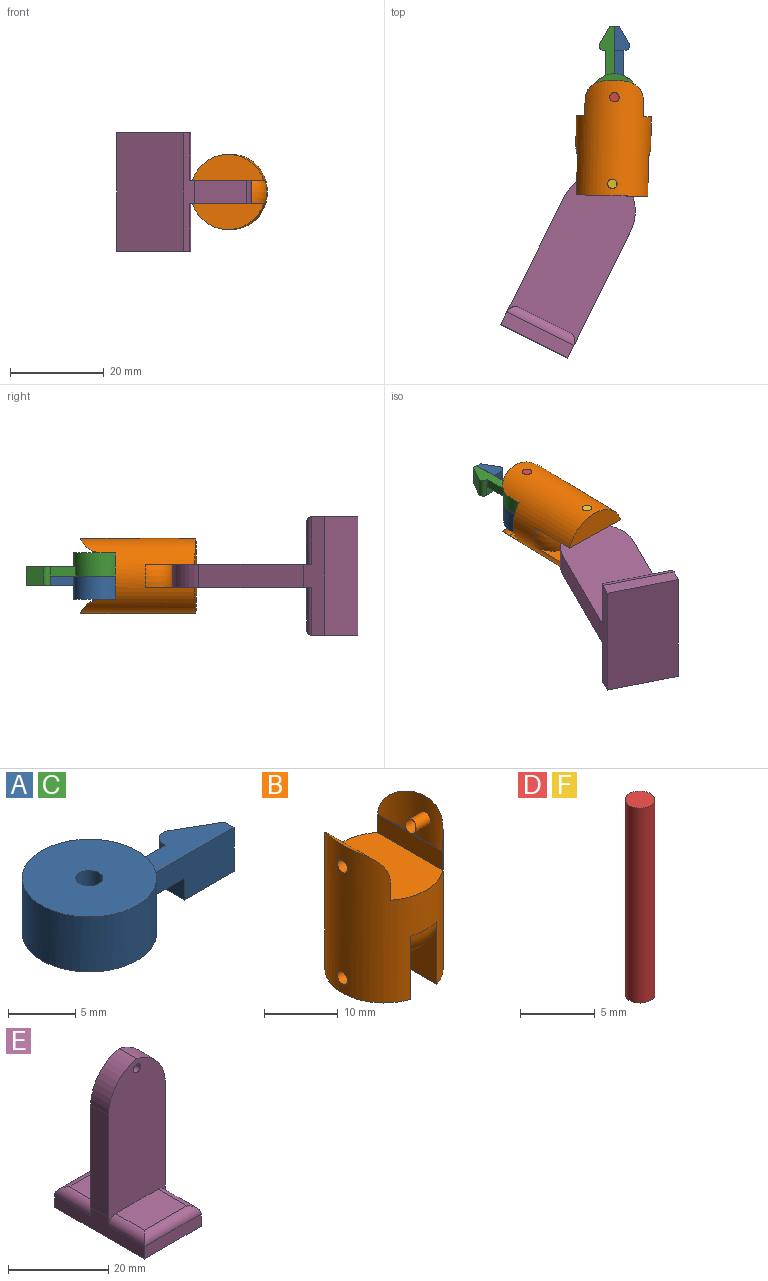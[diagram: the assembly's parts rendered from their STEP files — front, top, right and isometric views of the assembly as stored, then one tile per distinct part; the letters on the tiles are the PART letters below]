
ASSEMBLY  parts=6 mates=4
PART A: 12 faces, bbox 20.2x10x7 mm
  f0: plane 10.2x4mm, normal (0,-1,0), area 30.8mm2, adj f2,f3,f4,f6,f7,f9
  f1: plane 5.42x2mm, normal (0,1,0), area 10.8mm2, adj f2,f3,f4,f6
  f2: plane 10.61x3.27mm, normal (0,0,1), area 22.6mm2, adj f0,f1,f4,f6,f7,f8,f10
  f3: plane 15x10mm, normal (0,0,-1), area 85.7mm2, adj f0,f1,f4,f6,f11
  f4: cylinder r=5mm len=10mm, axis (0,0,-1), area 153mm2, adj f0,f1,f2,f3,f5
  f5: plane 10x10mm, normal (0,0,1), area 75.4mm2, adj f4,f11
  f6: plane 4x2.27mm, normal (-1,0,0), area 5.1mm2, adj f0,f1,f2,f3,f9,f10
  f7: plane 4x1mm, normal (1,0,0), area 4mm2, adj f0,f2,f8,f9
  f8: plane 4x3.7mm, normal (0.5,0.87,0), area 17.1mm2, adj f2,f7,f9,f10
  f9: plane 5.2x3.27mm, normal (0,0,-1), area 12.3mm2, adj f0,f6,f7,f8,f10
  f10: cylinder r=1mm len=4mm, axis (0,0,-1), area 8.4mm2, adj f2,f6,f8,f9
  f11: cylinder r=1mm len=5mm, axis (0,0,-1), area 31.4mm2, adj f3,f5
PART B: 19 faces, bbox 16x16x24.6 mm
  f0: cylinder r=8mm len=24.58mm, axis (0,0,-1), area 929mm2, adj f1,f2,f3,f5,f6,f7,f9,f10
  f1: cylinder r=1mm len=5.5mm, axis (1,0,0), area 34.4mm2, adj f0,f15
  f2: cylinder r=1mm len=5.44mm, axis (1,0,0), area 34.2mm2, adj f0,f6
  f3: cylinder r=1mm len=3mm, axis (-1,0,0), area 17.7mm2, adj f0,f4
  f4: cylinder r=5mm len=2mm, axis (0,1,0), area 3.2mm2, adj f3
  f5: plane 15.2x5.5mm, normal (0,0,-1), area 61.2mm2, adj f0,f6
  f6: plane 15.2x10.5mm, normal (-1,0,0), area 87mm2, adj f0,f2,f5,f7,f16
  f7: torus R=2.5mm, axis (0,0,-1), area 45.6mm2, adj f0,f6,f8,f15
  f8: plane 5x5mm, normal (0,0,-1), area 19.6mm2, adj f7,f16
  f9: cylinder r=5mm len=12.49mm, axis (0,-1,0), area 57.7mm2, adj f0,f10
  f10: plane 12.49x3mm, normal (-1,0,0), area 37.5mm2, adj f0,f9,f11
  f11: plane 16x10mm, normal (0,0,1), area 148.9mm2, adj f0,f10,f13
  f12: cylinder r=5mm len=12.49mm, axis (0,1,0), area 57.7mm2, adj f0,f13
  f13: plane 12.49x3mm, normal (1,0,0), area 37.5mm2, adj f0,f11,f12
  f14: plane 15.2x5.5mm, normal (0,0,-1), area 61.2mm2, adj f0,f15
  f15: plane 15.2x10.5mm, normal (1,0,0), area 87mm2, adj f0,f1,f7,f14,f16
  f16: torus R=2.5mm, axis (0,0,-1), area 45.6mm2, adj f0,f6,f8,f15
  f17: cylinder r=5mm len=2mm, axis (0,-1,0), area 3.2mm2, adj f18
  f18: cylinder r=1mm len=2.94mm, axis (-1,0,0), area 18.1mm2, adj f0,f17
PART C: same geometry as A
PART D: 3 faces, bbox 2x2x16 mm
  f0: cylinder r=1mm len=16mm, axis (0,0,-1), area 100.5mm2, adj f1,f2
  f1: plane 2x2mm, normal (0,0,1), area 3.1mm2, adj f0
  f2: plane 2x2mm, normal (0,0,-1), area 3.1mm2, adj f0
PART E: 20 faces, bbox 16x25.3x39.8 mm
  f0: plane 25.01x5.01mm, normal (1,0,0), area 125mm2, adj f1,f3,f5,f8
  f1: plane 36.8x16mm, normal (0,1,0), area 515.6mm2, adj f0,f2,f4,f5,f6,f7,f8,f10
  f2: plane 25.01x5.01mm, normal (-1,0,0), area 125mm2, adj f1,f3,f6,f10
  f3: plane 36.8x16mm, normal (0,-1,0), area 515.9mm2, adj f0,f2,f4,f5,f6,f8,f10,f13
  f4: cylinder r=1mm len=5mm, axis (0,1,0), area 31.4mm2, adj f1,f3
  f5: cylinder r=10mm len=9.8mm, axis (0,-1,0), area 68.5mm2, adj f0,f1,f3,f6
  f6: cylinder r=10mm len=9.8mm, axis (0,1,0), area 68.5mm2, adj f1,f2,f3,f5
  f7: plane 11.99x8.14mm, normal (0,0,1), area 97.6mm2, adj f1,f14,f15,f16
  f8: plane 25.29x5.01mm, normal (1,0,0), area 85.8mm2, adj f0,f1,f3,f9,f11,f12,f14,f17
  f9: plane 15.99x3mm, normal (0,1,0), area 48mm2, adj f8,f10,f12,f15
  f10: plane 25.29x5.01mm, normal (-1,0,0), area 85.8mm2, adj f1,f2,f3,f9,f11,f12,f16,f19
  f11: plane 15.99x3mm, normal (0,-1,0), area 48mm2, adj f8,f10,f12,f18
  f12: plane 25.28x15.99mm, normal (0,0,-1), area 404.2mm2, adj f8,f9,f10,f11
  f13: plane 11.99x8.14mm, normal (0,0,1), area 97.6mm2, adj f3,f17,f18,f19
  f14: cylinder r=2mm len=10.14mm, axis (0,1,0), area 28.7mm2, adj f1,f7,f8,f15
  f15: cylinder r=2mm len=15.99mm, axis (-1,0,0), area 44mm2, adj f7,f9,f14,f16
  f16: cylinder r=2mm len=10.14mm, axis (0,-1,0), area 28.7mm2, adj f1,f7,f10,f15
  f17: cylinder r=2mm len=10.14mm, axis (0,1,0), area 28.7mm2, adj f3,f8,f13,f18
  f18: cylinder r=2mm len=15.99mm, axis (1,0,0), area 44mm2, adj f11,f13,f17,f19
  f19: cylinder r=2mm len=10.14mm, axis (0,-1,0), area 28.7mm2, adj f3,f10,f13,f18
PART F: same geometry as D
PLACE A rot(axis=(0.71,0.71,0),180deg) t=(-2.76,7.62,48.58)mm
PLACE B rot(axis=(-0.58,-0.57,-0.58),120.8deg) t=(-3.26,-13.37,48.58)mm fixed
PLACE C rot(axis=(0,0,1),90deg) t=(-2.76,7.62,48.58)mm
PLACE D t=(-2.76,7.62,40.58)mm fixed
PLACE E rot(axis=(-0.95,0.22,-0.22),93deg) t=(-17.65,-39.94,48.58)mm
PLACE F t=(-3.2,-10.87,40.58)mm
MATE revolute C.f4 <-> D.f0  axis (0,0,-1) through (-2.76,7.62,48.58)mm
MATE revolute E.f4 <-> F.f0  axis (0,0,-1) through (-3.2,-10.87,48.58)mm
MATE revolute A.f4 <-> D.f0  axis (0,0,1) through (-2.76,7.62,48.58)mm
MATE revolute E.f4 <-> B.f1  axis (0,0,-1) through (-3.2,-10.87,46.08)mm
